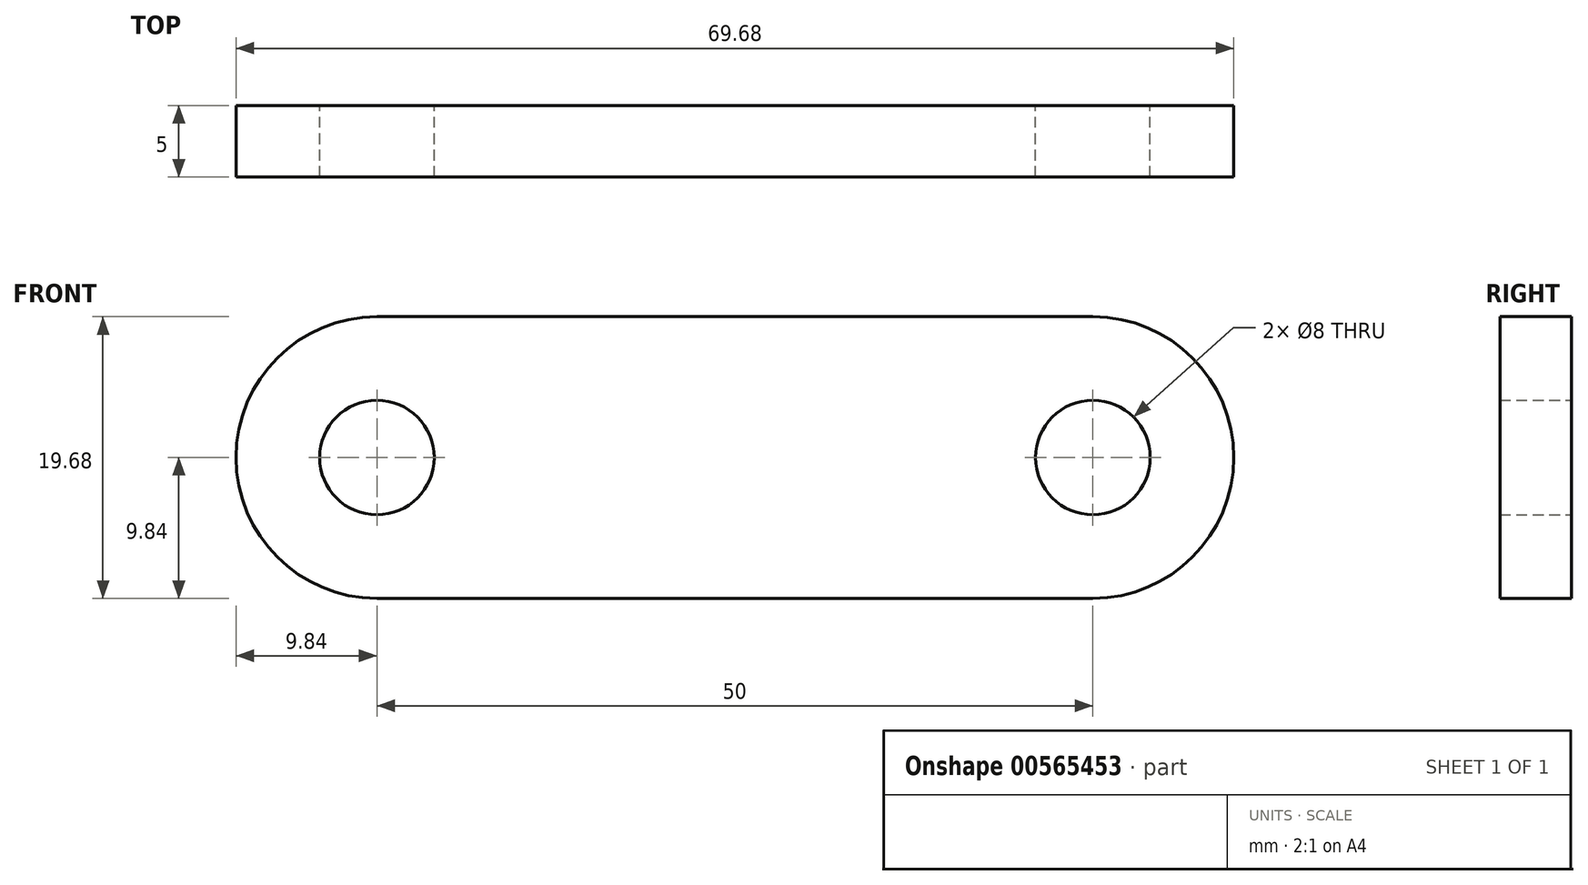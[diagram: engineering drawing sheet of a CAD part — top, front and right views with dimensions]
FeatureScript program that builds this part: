
annotation { "Feature Type Name" : "Feature", "Feature Type Description" : "" }
export const myFeature = defineFeature(function(context is Context, id is Id, definition is map)
    precondition{}
    {
        {
            var Q0;
            Q0=qCreatedBy(makeId("Front.planeOp"),FACE);
            var sketch = newSketch(context, id + "F0", { "sketchPlane" : qUnion([Q0])});
            skArc(sketch, "E0", {"start": v(-25, 9.84) * mm, "mid": v(-34.84, 0) * mm, "end": v(-25, -9.84) * mm});
            skLineSegment(sketch, "E1", {"start": v(-25, 9.84) * mm, "end": v(0, 9.84) * mm});
            skLineSegment(sketch, "E2", {"start": v(-25, -9.84) * mm, "end": v(0, -9.83) * mm});
            skArc(sketch, "E3.MirrorCS", {"start": v(25, 9.84) * mm, "mid": v(34.84, 0) * mm, "end": v(25, -9.84) * mm});
            skLineSegment(sketch, "E4.MirrorCS", {"start": v(25, 9.84) * mm, "end": v(0, 9.84) * mm});
            skLineSegment(sketch, "E5.MirrorCS", {"start": v(25, -9.84) * mm, "end": v(0, -9.83) * mm});
            skCircle(sketch, "E6", {"center": v(-25, 0) * mm, "radius": 4 * mm});
            skCircle(sketch, "E7", {"center": v(25, 0) * mm, "radius": 4 * mm});
            skSolve(sketch);
        }
        {
            var Q0;
            Q0 = qSketchRegion(id + "F0", true);
            extrude(context, id + "F1", {"entities" : qUnion([Q0]), "endBound" : BoundingType.SYMMETRIC, "depth" : 5 * mm, "offsetDistance" : 25.4 * mm});
        }
    });
